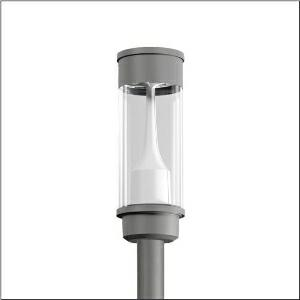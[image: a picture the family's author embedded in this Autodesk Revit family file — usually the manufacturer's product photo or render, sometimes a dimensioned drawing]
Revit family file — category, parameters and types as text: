
# Revit family: litepole_iq___p1_0a_5xa5415bf14hp_4130
name_source: partatom
category: Lighting Fixtures
units: mm (PartAtom-declared; Revit-internal decimal feet)

## family parameters
Cut with Voids When Loaded = No
Host = Face
Light Source = No
Part Type = Normal
Room Calculation Point = No
Round Connector Dimension = Use Diameter
Shared = No

## types (1)
- --- (1 x LED, 3890 lm, 33.6 W, 2200K)
    Apparent Load = 34 VA
    CIE Flux Codes = 31 60 90 94 100
    Color Rendering = 70
    Color Temperature = 2200K
    Default Elevation = 1800 mm
    Description = Litepole iQ, mast luminaire, Module 540 iQ-SR, primary light control with 3 zone facetted reflector, of plastic, silver coated, highly specular, structured, primary optical cover: cover, of PMMA, transparent, partly coated, light distribution: P1.0a, light emission: direct distribution, primary light characteristic: strongly asymmetric, installation type: post-top, LED, High Power LED, rated luminous flux: 3.890lm, luminous efficacy: 116lm/W, light colour: 722, colour temperature: 2200K, control gear: iQ Street-Remote, control: optimised constant luminous flux control (CLO 2.0), Desk-Remote (wireless, voltage-free reading and setting of iQ features in the workshop via application-optimized NFC function/RFID function), Light-Fading, Smart-Wire, Night-Set, Lumen-Switch, Temp-Guard, Auto-Match, Street-Remote, pre-setting: logarithmic dimming characteristic, with terminal, 6-pole, max. 2.5mm², mains connection: 230..240V, AC, 50/60Hz, start of lifetime: 34W, end of service life: 36W, reduction: 15W, luminaire housing, upper part, of glass-fibre reinforced polyester, coated, Siteco® metallic grey (DB 702S), diameter: 210mm, height: 590mm, spigot size: d x l = 76 x 70mm (post-top) | with reducer (optional accessory) 60 x 70mm, mounting height: 3..5m, post-top mast mounting element, of diecast aluminium, coated, Siteco® metallic grey (DB 702S), Module 540 iQ-SR, traffic white (RAL 9016), equipment: Power, protection rating (complete): IP65, insulation class (complete): insulation class II (safety insulation), certification: CE, ENEC, VDE, packaging unit: 1 piece

Light Distribution: P1.0a
    Height = 590 mm
    Lamp = 1 x LED
    Lamp Light Flux = 3890 lm
    Lamp Power = 33.6 W
    Lamp count = 1
    Length = 220 mm
    Luminous efficacy = 116 lm/W
    Manufacturer = Siteco
    ModVariant = No
    Model = 5XA5415BF14HP
    Number of Poles = 1
    OnlyDefault = Yes
    Power Factor = 1
    Product Name = Litepole iQ | P1.0a
    Product group = mast luminaire | pylon top
    ProductGroupID = 6100
    Protection Class = Protection class II
    Protection Degree = IP 65
    RLX_Detail_Level = 1
    RLX_Emergency_Light_Flux = 0 lm
    RLX_Emergency_Type = 0
    RLX_Emergency_Type_DB = No
    RlxData = <blob elided: 29953 chars, md5=c8892315>
    Socket = socket
    Standby Power = 0 W
    System Light Flux = 3890 lm
    System Power = 34 W
    Type Comments = factory setting: luminous flux: 100 % | dim-lin: 254 | 695 mA
    Type Image = l_1006025.jpg
    URL = http://relux.com
    VarID = @adj_216273
    Voltage = 0 V
    Weight = 0.00 kg
    Width = 0 mm  [stored 0 ft]

note: [stored X ft] marks values corroborated as IEEE doubles in the binary element streams (Revit-internal decimal feet)

## geometry (parser evidence)
native form markers: Blend x4, Sweep x12
no freeform markers — native parametric forms only
